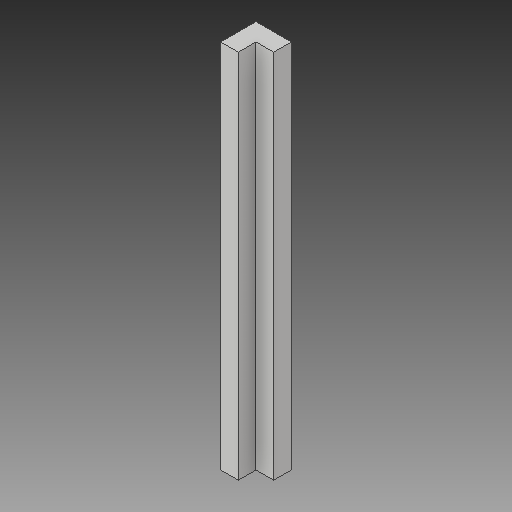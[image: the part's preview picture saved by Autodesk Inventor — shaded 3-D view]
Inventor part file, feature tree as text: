
AUTODESK INVENTOR PART (.ipt)
format: ipt  version: 2017 (Build 210142000, 142)  size: 84,992 bytes
history: native  units: in
note: dims shown in document units (in); Inventor stores cm internally (conversion verified against a paired STEP export)
features: other x3, sketch x3
ambient origin geometry x8: Origin, YZ Plane, XZ Plane, XY Plane, X Axis, Y Axis, Z Axis, Center Point
bodies: Solid1 (feature_tree)
feature tree (6):
  other  "rev1 corners.ipt"
  other  "Solid1::rev1 corners.ipt"
  other  "TaggingFeature1"
  sketch  "Sketch1"  dims[d0=0.3937in]
  sketch  "Sketch2"
  sketch  "Sketch3"
